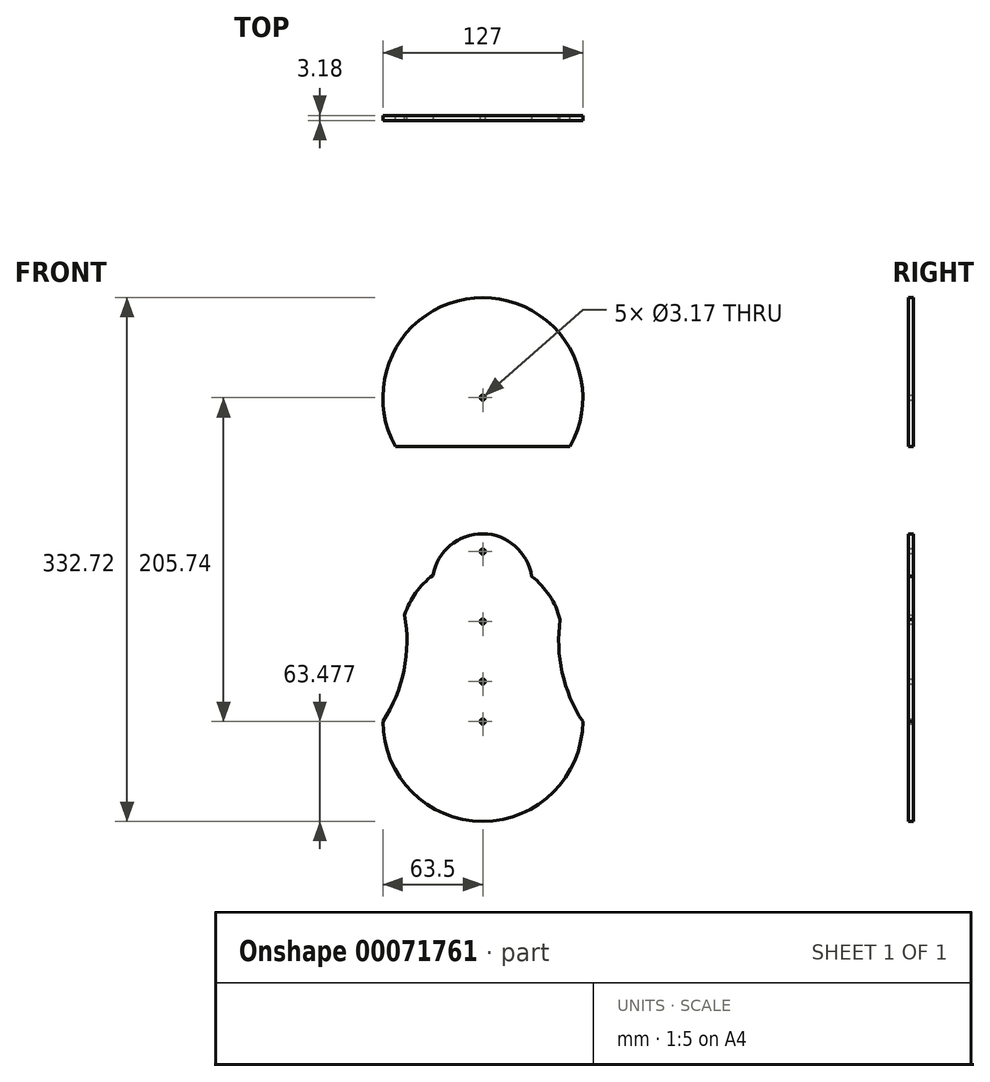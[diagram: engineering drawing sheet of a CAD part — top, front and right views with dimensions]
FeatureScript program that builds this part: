
annotation { "Feature Type Name" : "Feature", "Feature Type Description" : "" }
export const myFeature = defineFeature(function(context is Context, id is Id, definition is map)
    precondition{}
    {
        {
            var Q0;
            Q0=qCreatedBy(makeId("Front.planeOp"),FACE);
            var sketch = newSketch(context, id + "F0", { "sketchPlane" : qUnion([Q0])});
            skPoint(sketch, "E0.rect.middle", {"position": v(0, 0) * mm});
            skArc(sketch, "E1", {"start": v(63.5, 102.86) * mm, "mid": v(0, 166.36) * mm, "end": v(-63.5, 102.86) * mm});
            skArc(sketch, "E2", {"start": v(-63.5, -102.86) * mm, "mid": v(0, -166.36) * mm, "end": v(63.5, -102.86) * mm});
            skArc(sketch, "E3", {"start": v(-49.6, 35.1) * mm, "mid": v(-50.1, 70.3) * mm, "end": v(-63.5, 102.86) * mm});
            skArc(sketch, "E4", {"start": v(-63.5, -102.86) * mm, "mid": v(-50.1, -70.3) * mm, "end": v(-49.6, -35.1) * mm});
            skArc(sketch, "E5", {"start": v(63.5, 102.86) * mm, "mid": v(50.42, 71.84) * mm, "end": v(49.12, 38.2) * mm});
            skArc(sketch, "E6", {"start": v(49.12, -38.2) * mm, "mid": v(50.42, -71.84) * mm, "end": v(63.5, -102.86) * mm});
            skArc(sketch, "E7", {"start": v(48.18, -51.43) * mm, "mid": v(50.27, 0) * mm, "end": v(48.18, 51.43) * mm});
            skArc(sketch, "E8", {"start": v(-48.23, 54.55) * mm, "mid": v(-50.58, 0) * mm, "end": v(-48.23, -54.55) * mm});
            skPoint(sketch, "E9.orphan", {"position": v(-63.5, 0) * mm});
            skPoint(sketch, "E10.orphan", {"position": v(63.5, 0) * mm});
            skSolve(sketch);
        }
        {
            var Q0;
            {var subQ4=sQuery(id+"F0.wireOp",EDGE,"E1");Q0=makeQuery(id+"F0.imprint","IMPRINT",FACE,{"disambiguationData":[TD([[makeQuery(id+"F0.imprint","IMPRINT",EDGE,{"derivedFrom":subQ4}),1.0]])]});}
            extrude(context, id + "F1", {"entities" : qUnion([Q0]), "depth" : 3.17 * mm});
        }
        {
            var Q0;
            Q0=makeQuery(id+"F1.opExtrude","CAP_FACE",FACE,{"disambiguationData":[OSD([sQuery(id+"F0.wireOp",EDGE,"E1"),sQuery(id+"F0.wireOp",EDGE,"E2"),sQuery(id+"F0.wireOp",EDGE,"E3"),sQuery(id+"F0.wireOp",EDGE,"E4"),sQuery(id+"F0.wireOp",EDGE,"E5"),sQuery(id+"F0.wireOp",EDGE,"E6"),sQuery(id+"F0.wireOp",EDGE,"E7"),sQuery(id+"F0.wireOp",EDGE,"E8")])],"isStart":false});
            var sketch = newSketch(context, id + "F2", { "sketchPlane" : qUnion([Q0])});
            skArc(sketch, "E11.0", {"start": v(63.5, 102.86) * mm, "mid": v(0, 166.36) * mm, "end": v(-63.5, 102.86) * mm});
            skArc(sketch, "E12.0", {"start": v(-63.5, -102.86) * mm, "mid": v(0, -166.36) * mm, "end": v(63.5, -102.86) * mm});
            skCircle(sketch, "E13", {"center": v(0, 102.86) * mm, "radius": 31.75 * mm});
            skSolve(sketch);
        }
        {
            var Q0;
            Q0=makeQuery(id+"F2.imprint","IMPRINT",FACE,{"disambiguationData":[TD([[makeQuery(id+"F2.imprint","IMPRINT",EDGE,{"derivedFrom":sQuery(id+"F2.wireOp",EDGE,"E11.0")}),1.0]])]});
            var sketch = newSketch(context, id + "F3", { "sketchPlane" : qUnion([Q0])});
            skCircle(sketch, "E14.0", {"center": v(0, 102.86) * mm, "radius": 31.75 * mm});
            skCircle(sketch, "E15", {"center": v(0, 58.4) * mm, "radius": 12.7 * mm});
            skSolve(sketch);
        }
        {
            var Q0;
            Q0=makeQuery(id+"F2.imprint","IMPRINT",FACE,{"disambiguationData":[TD([[makeQuery(id+"F2.imprint","IMPRINT",EDGE,{"derivedFrom":sQuery(id+"F2.wireOp",EDGE,"E13")}),1.0]])]});
            extrude(context, id + "F4", {"entities" : qUnion([Q0]), "depth" : 6.35 * mm});
        }
        {
            var Q0;
            Q0=makeQuery(id+"F3.imprint","IMPRINT",FACE,{"disambiguationData":[TD([[makeQuery(id+"F3.imprint","IMPRINT",EDGE,{"derivedFrom":sQuery(id+"F3.wireOp",EDGE,"E15")}),1.0]])]});
            extrude(context, id + "F5", {"entities" : qUnion([Q0]), "depth" : 6.35 * mm});
        }
        {
            var Q0;
            Q0=makeQuery(id+"F5.opExtrude","CAP_FACE",FACE,{"disambiguationData":[OSD([sQuery(id+"F3.wireOp",EDGE,"E15")])],"isStart":false});
            var sketch = newSketch(context, id + "F6", { "sketchPlane" : qUnion([Q0])});
            skCircle(sketch, "E16.0", {"center": v(0, 58.4) * mm, "radius": 12.7 * mm});
            skCircle(sketch, "E17", {"center": v(0, 58.4) * mm, "radius": 40.64 * mm});
            skSolve(sketch);
        }
        {
            var Q0;
            Q0=makeQuery(id+"F6.imprint","IMPRINT",FACE,{"disambiguationData":[TD([[makeQuery(id+"F6.imprint","IMPRINT",EDGE,{"derivedFrom":sQuery(id+"F6.wireOp",EDGE,"E16.0")}),-1.0]])]});
            var Q1;
            Q1=makeQuery(id+"F6.imprint","IMPRINT",FACE,{"disambiguationData":[TD([[makeQuery(id+"F6.imprint","IMPRINT",EDGE,{"derivedFrom":sQuery(id+"F6.wireOp",EDGE,"E16.0")}),1.0]])]});
            extrude(context, id + "F7", {"entities" : qUnion([Q0, Q1]), "depth" : 6.35 * mm});
        }
        {
            var Q0;
            Q0=makeQuery(id+"F7.opExtrude","CAP_FACE",FACE,{"disambiguationData":[OSD([sQuery(id+"F6.wireOp",EDGE,"E17")])],"isStart":true});
            var sketch = newSketch(context, id + "F8", { "sketchPlane" : qUnion([Q0])});
            skCircle(sketch, "E18.0", {"center": v(0, 58.4) * mm, "radius": 40.64 * mm});
            skCircle(sketch, "E19", {"center": v(0, 5.07) * mm, "radius": 12.7 * mm});
            skSolve(sketch);
        }
        {
            var Q0;
            Q0=makeQuery(id+"F8.imprint","IMPRINT",FACE,{"disambiguationData":[TD([[makeQuery(id+"F8.imprint","IMPRINT",EDGE,{"derivedFrom":sQuery(id+"F8.wireOp",EDGE,"E19")}),1.0]])]});
            extrude(context, id + "F9", {"entities" : qUnion([Q0]), "operationType" : NewBodyOperationType.ADD, "oppositeDirection" : true, "depth" : 6.35 * mm});
        }
        {
            var Q0;
            Q0=makeQuery(id+"F9.opExtrude","CAP_FACE",FACE,{"disambiguationData":[OSD([sQuery(id+"F8.wireOp",EDGE,"E19")])],"isStart":true});
            var sketch = newSketch(context, id + "F10", { "sketchPlane" : qUnion([Q0])});
            skCircle(sketch, "E20", {"center": v(0, 5.07) * mm, "radius": 31.75 * mm});
            skSolve(sketch);
        }
        {
            var Q0;
            Q0=makeQuery(id+"F10.imprint","IMPRINT",FACE,{"disambiguationData":[TD([[makeQuery(id+"F10.imprint","IMPRINT",EDGE,{"derivedFrom":sQuery(id+"F10.wireOp",EDGE,"E20")}),1.0]])]});
            var Q1;
            Q1=makeQuery(id+"F10.imprint","IMPRINT",FACE,{"disambiguationData":[TD([[makeQuery(id+"F10.imprint","IMPRINT",EDGE,{"derivedFrom":makeQuery(id+"F9.opExtrude","CAP_EDGE",EDGE,{"disambiguationData":[OSD([sQuery(id+"F8.wireOp",EDGE,"E19")])],"isStart":true})}),1.0]])]});
            extrude(context, id + "F11", {"entities" : qUnion([Q0, Q1]), "depth" : 6.35 * mm});
        }
        {
            var Q0;
            Q0=makeQuery(id+"F1.opExtrude","CAP_FACE",FACE,{"disambiguationData":[OSD([sQuery(id+"F0.wireOp",EDGE,"E1"),sQuery(id+"F0.wireOp",EDGE,"E2"),sQuery(id+"F0.wireOp",EDGE,"E3"),sQuery(id+"F0.wireOp",EDGE,"E4"),sQuery(id+"F0.wireOp",EDGE,"E5"),sQuery(id+"F0.wireOp",EDGE,"E6"),sQuery(id+"F0.wireOp",EDGE,"E7"),sQuery(id+"F0.wireOp",EDGE,"E8")])],"isStart":false});
            var sketch = newSketch(context, id + "F12", { "sketchPlane" : qUnion([Q0])});
            skCircle(sketch, "E21.0", {"center": v(0, 5.07) * mm, "radius": 12.7 * mm});
            skCircle(sketch, "E22", {"center": v(0, -39.38) * mm, "radius": 12.7 * mm});
            skSolve(sketch);
        }
        {
            var Q0;
            Q0=makeQuery(id+"F12.imprint","IMPRINT",FACE,{"disambiguationData":[TD([[makeQuery(id+"F12.imprint","IMPRINT",EDGE,{"derivedFrom":sQuery(id+"F12.wireOp",EDGE,"E22")}),1.0]])]});
            extrude(context, id + "F13", {"entities" : qUnion([Q0]), "depth" : 6.35 * mm});
        }
        {
            var Q0;
            Q0=makeQuery(id+"F13.opExtrude","CAP_FACE",FACE,{"disambiguationData":[OSD([sQuery(id+"F12.wireOp",EDGE,"E22")])],"isStart":false});
            var sketch = newSketch(context, id + "F14", { "sketchPlane" : qUnion([Q0])});
            skCircle(sketch, "E23", {"center": v(0, -39.38) * mm, "radius": 25.4 * mm});
            skSolve(sketch);
        }
        {
            var Q0;
            Q0=makeQuery(id+"F14.imprint","IMPRINT",FACE,{"disambiguationData":[TD([[makeQuery(id+"F14.imprint","IMPRINT",EDGE,{"derivedFrom":sQuery(id+"F14.wireOp",EDGE,"E23")}),1.0]])]});
            var Q1;
            Q1=makeQuery(id+"F14.imprint","IMPRINT",FACE,{"disambiguationData":[TD([[makeQuery(id+"F14.imprint","IMPRINT",EDGE,{"derivedFrom":makeQuery(id+"F13.opExtrude","CAP_EDGE",EDGE,{"disambiguationData":[OSD([sQuery(id+"F12.wireOp",EDGE,"E22")])],"isStart":false})}),1.0]])]});
            extrude(context, id + "F15", {"entities" : qUnion([Q0, Q1]), "depth" : 6.35 * mm});
        }
        {
            var Q0;
            Q0=makeQuery(id+"F15.opExtrude","CAP_FACE",FACE,{"disambiguationData":[OSD([sQuery(id+"F14.wireOp",EDGE,"E23")])],"isStart":true});
            var sketch = newSketch(context, id + "F16", { "sketchPlane" : qUnion([Q0])});
            skCircle(sketch, "E24.0", {"center": v(0, -39.38) * mm, "radius": 25.4 * mm});
            skCircle(sketch, "E25", {"center": v(0, -77.48) * mm, "radius": 12.7 * mm});
            skSolve(sketch);
        }
        {
            var Q0;
            Q0=makeQuery(id+"F16.imprint","IMPRINT",FACE,{"disambiguationData":[TD([[makeQuery(id+"F16.imprint","IMPRINT",EDGE,{"derivedFrom":sQuery(id+"F16.wireOp",EDGE,"E25")}),1.0]])]});
            extrude(context, id + "F17", {"entities" : qUnion([Q0]), "oppositeDirection" : true, "depth" : 6.35 * mm});
        }
        {
            var Q0;
            Q0=makeQuery(id+"F17.opExtrude","CAP_FACE",FACE,{"disambiguationData":[OSD([sQuery(id+"F16.wireOp",EDGE,"E25")])],"isStart":true});
            var sketch = newSketch(context, id + "F18", { "sketchPlane" : qUnion([Q0])});
            skCircle(sketch, "E26.0", {"center": v(0, -77.48) * mm, "radius": 12.7 * mm});
            skCircle(sketch, "E27", {"center": v(0, -102.88) * mm, "radius": 12.7 * mm});
            skSolve(sketch);
        }
        {
            var Q0;
            Q0=makeQuery(id+"F18.imprint","IMPRINT",FACE,{"disambiguationData":[TD([[makeQuery(id+"F18.imprint","IMPRINT",EDGE,{"derivedFrom":sQuery(id+"F18.wireOp",EDGE,"E27")}),1.0]])]});
            extrude(context, id + "F19", {"entities" : qUnion([Q0]), "oppositeDirection" : true, "depth" : 6.35 * mm});
        }
        {
            var Q0;
            Q0=makeQuery(id+"F1.opExtrude","CAP_FACE",FACE,{"disambiguationData":[OSD([sQuery(id+"F0.wireOp",EDGE,"E1"),sQuery(id+"F0.wireOp",EDGE,"E2"),sQuery(id+"F0.wireOp",EDGE,"E3"),sQuery(id+"F0.wireOp",EDGE,"E4"),sQuery(id+"F0.wireOp",EDGE,"E5"),sQuery(id+"F0.wireOp",EDGE,"E6"),sQuery(id+"F0.wireOp",EDGE,"E7"),sQuery(id+"F0.wireOp",EDGE,"E8")])],"isStart":false});
            var sketch = newSketch(context, id + "F20", { "sketchPlane" : qUnion([Q0])});
            skCircle(sketch, "E28.0", {"center": v(0, -77.48) * mm, "radius": 12.7 * mm});
            skCircle(sketch, "E29", {"center": v(0, -77.48) * mm, "radius": 6.35 * mm});
            skCircle(sketch, "E30.0", {"center": v(0, -102.88) * mm, "radius": 12.7 * mm});
            skCircle(sketch, "E31", {"center": v(0, -102.88) * mm, "radius": 6.35 * mm});
            skSolve(sketch);
        }
        {
            var Q0;
            Q0=makeQuery(id+"F20.imprint","IMPRINT",FACE,{"disambiguationData":[TD([[makeQuery(id+"F20.imprint","IMPRINT",EDGE,{"derivedFrom":sQuery(id+"F20.wireOp",EDGE,"E29")}),1.0]])]});
            var Q1;
            Q1=makeQuery(id+"F20.imprint","IMPRINT",FACE,{"disambiguationData":[TD([[makeQuery(id+"F20.imprint","IMPRINT",EDGE,{"derivedFrom":sQuery(id+"F20.wireOp",EDGE,"E31")}),1.0]])]});
            extrude(context, id + "F21", {"entities" : qUnion([Q0, Q1]), "depth" : 6.35 * mm});
        }
        {
            var Q0;
            Q0=makeQuery(id+"F1.opExtrude","CAP_FACE",FACE,{"disambiguationData":[OSD([sQuery(id+"F0.wireOp",EDGE,"E1"),sQuery(id+"F0.wireOp",EDGE,"E2"),sQuery(id+"F0.wireOp",EDGE,"E3"),sQuery(id+"F0.wireOp",EDGE,"E4"),sQuery(id+"F0.wireOp",EDGE,"E5"),sQuery(id+"F0.wireOp",EDGE,"E6"),sQuery(id+"F0.wireOp",EDGE,"E7"),sQuery(id+"F0.wireOp",EDGE,"E8")])],"isStart":true});
            var sketch = newSketch(context, id + "F22", { "sketchPlane" : qUnion([Q0])});
            skCircle(sketch, "E32", {"center": v(0, 102.86) * mm, "radius": 1.59 * mm});
            skCircle(sketch, "E33", {"center": v(0, 58.4) * mm, "radius": 1.59 * mm});
            skCircle(sketch, "E34", {"center": v(0, 5.07) * mm, "radius": 1.59 * mm});
            skCircle(sketch, "E35", {"center": v(0, -39.38) * mm, "radius": 1.59 * mm});
            skCircle(sketch, "E36", {"center": v(0, -77.48) * mm, "radius": 1.59 * mm});
            skCircle(sketch, "E37", {"center": v(0, -102.88) * mm, "radius": 1.59 * mm});
            skSolve(sketch);
        }
        {
            var Q0;
            Q0=qSketchRegion(id+"F22",true);
            extrude(context, id + "F23", {"entities" : qUnion([Q0]), "operationType" : NewBodyOperationType.REMOVE, "endBound" : BoundingType.THROUGH_ALL, "oppositeDirection" : true, "depth" : 25.4 * mm});
        }
        {
            var Q0;
            Q0=makeQuery(id+"F1.opExtrude","CAP_FACE",FACE,{"disambiguationData":[OSD([sQuery(id+"F0.wireOp",EDGE,"E1"),sQuery(id+"F0.wireOp",EDGE,"E2"),sQuery(id+"F0.wireOp",EDGE,"E3"),sQuery(id+"F0.wireOp",EDGE,"E4"),sQuery(id+"F0.wireOp",EDGE,"E5"),sQuery(id+"F0.wireOp",EDGE,"E6"),sQuery(id+"F0.wireOp",EDGE,"E7"),sQuery(id+"F0.wireOp",EDGE,"E8")])],"isStart":true});
            var sketch = newSketch(context, id + "F24", { "sketchPlane" : qUnion([Q0])});
            skLineSegment(sketch, "E38", {"start": v(-50.42, 71.84) * mm, "end": v(50.42, 71.84) * mm});
            skLineSegment(sketch, "E39", {"start": v(-50.27, 0) * mm, "end": v(50.58, 0) * mm});
            skSolve(sketch);
        }
        {
            var Q0;
            Q0=makeQuery(id+"F4.opExtrude","SWEPT_BODY",BODY,{"disambiguationData":[OSD([sQuery(id+"F2.wireOp",EDGE,"E13")])]});
            deleteBodies(context, id + "F25", {"entities" : qUnion([Q0])});
        }
        {
            var Q0;
            Q0=makeQuery(id+"F7.opExtrude","SWEPT_BODY",BODY,{"disambiguationData":[OSD([sQuery(id+"F6.wireOp",EDGE,"E17")])]});
            deleteBodies(context, id + "F26", {"entities" : qUnion([Q0])});
        }
        {
            var Q0;
            Q0=makeQuery(id+"F5.opExtrude","SWEPT_BODY",BODY,{"disambiguationData":[OSD([sQuery(id+"F3.wireOp",EDGE,"E15")])]});
            deleteBodies(context, id + "F27", {"entities" : qUnion([Q0])});
        }
        {
            var Q0;
            Q0=makeQuery(id+"F9.opExtrude","SWEPT_BODY",BODY,{"disambiguationData":[OSD([sQuery(id+"F8.wireOp",EDGE,"E19")])]});
            deleteBodies(context, id + "F28", {"entities" : qUnion([Q0])});
        }
        {
            var Q0;
            Q0=makeQuery(id+"F11.opExtrude","SWEPT_BODY",BODY,{"disambiguationData":[OSD([sQuery(id+"F10.wireOp",EDGE,"E20")])]});
            deleteBodies(context, id + "F29", {"entities" : qUnion([Q0])});
        }
        {
            var Q0;
            Q0=makeQuery(id+"F15.opExtrude","SWEPT_BODY",BODY,{"disambiguationData":[OSD([sQuery(id+"F14.wireOp",EDGE,"E23")])]});
            deleteBodies(context, id + "F30", {"entities" : qUnion([Q0])});
        }
        {
            var Q0;
            Q0=makeQuery(id+"F13.opExtrude","SWEPT_BODY",BODY,{"disambiguationData":[OSD([sQuery(id+"F12.wireOp",EDGE,"E22")])]});
            deleteBodies(context, id + "F31", {"entities" : qUnion([Q0])});
        }
        {
            var Q0;
            Q0=makeQuery(id+"F17.opExtrude","SWEPT_BODY",BODY,{"disambiguationData":[OSD([sQuery(id+"F16.wireOp",EDGE,"E25")])]});
            deleteBodies(context, id + "F32", {"entities" : qUnion([Q0])});
        }
        {
            var Q0;
            Q0=makeQuery(id+"F21.opExtrude","SWEPT_BODY",BODY,{"disambiguationData":[OSD([sQuery(id+"F20.wireOp",EDGE,"E29")])]});
            deleteBodies(context, id + "F33", {"entities" : qUnion([Q0])});
        }
        {
            var Q0;
            Q0=makeQuery(id+"F19.opExtrude","SWEPT_BODY",BODY,{"disambiguationData":[OSD([sQuery(id+"F18.wireOp",EDGE,"E27")])]});
            deleteBodies(context, id + "F34", {"entities" : qUnion([Q0])});
        }
        {
            var Q0;
            Q0=makeQuery(id+"F21.opExtrude","SWEPT_BODY",BODY,{"disambiguationData":[OSD([sQuery(id+"F20.wireOp",EDGE,"E31")])]});
            deleteBodies(context, id + "F35", {"entities" : qUnion([Q0])});
        }
        {
            var Q0;
            {var subQ4=sQuery(id+"F24.wireOp",EDGE,"E38");Q0=makeQuery(id+"F24.imprint","IMPRINT",FACE,{"disambiguationData":[TD([[makeQuery(id+"F24.imprint","IMPRINT",EDGE,{"derivedFrom":subQ4}),-1.0]])]});}
            extrude(context, id + "F36", {"entities" : qUnion([Q0]), "operationType" : NewBodyOperationType.REMOVE, "oppositeDirection" : true, "depth" : 25.4 * mm});
        }
        {
            var Q0;
            {var subQ0=sQuery(id+"F0.wireOp",EDGE,"E6");var subQ1=sQuery(id+"F0.wireOp",EDGE,"E4");var subQ2=sQuery(id+"F0.wireOp",EDGE,"E7");var subQ3=sQuery(id+"F0.wireOp",EDGE,"E2");var subQ4=sQuery(id+"F0.wireOp",EDGE,"E8");Q0=makeQuery(id+"F36.boolean.opBoolean","SPLIT",FACE,{"disambiguationData":[TD([makeQuery(id+"F1.opExtrude","SWEPT_FACE",FACE,{"disambiguationData":[OSD([subQ3])]})])],"derivedFrom":makeQuery(id+"F1.opExtrude","CAP_FACE",FACE,{"disambiguationData":[OSD([sQuery(id+"F0.wireOp",EDGE,"E1"),subQ3,sQuery(id+"F0.wireOp",EDGE,"E3"),subQ1,sQuery(id+"F0.wireOp",EDGE,"E5"),subQ0,subQ2,subQ4])],"isStart":true})});}
            var sketch = newSketch(context, id + "F37", { "sketchPlane" : qUnion([Q0])});
            skArc(sketch, "E40", {"start": v(0.16, 0) * mm, "mid": v(-31.03, -10.65) * mm, "end": v(-49.12, -38.2) * mm});
            skArc(sketch, "E41", {"start": v(49.6, -35.1) * mm, "mid": v(30.7, -9.37) * mm, "end": v(0.16, 0) * mm});
            skSolve(sketch);
        }
        {
            var Q0;
            {var subQ1=makeQuery(id+"F1.opExtrude","CAP_EDGE",EDGE,{"disambiguationData":[OSD([sQuery(id+"F0.wireOp",EDGE,"E7")])],"isStart":true});Q0=makeQuery(id+"F37.imprint","IMPRINT",FACE,{"disambiguationData":[TD([[makeQuery(id+"F37.imprint","IMPRINT",EDGE,{"derivedFrom":subQ1}),-1.0]])]});}
            var Q1;
            {var subQ1=makeQuery(id+"F1.opExtrude","CAP_EDGE",EDGE,{"disambiguationData":[OSD([sQuery(id+"F0.wireOp",EDGE,"E8")])],"isStart":true});Q1=makeQuery(id+"F37.imprint","IMPRINT",FACE,{"disambiguationData":[TD([[makeQuery(id+"F37.imprint","IMPRINT",EDGE,{"derivedFrom":subQ1}),-1.0]])]});}
            extrude(context, id + "F38", {"entities" : qUnion([Q0, Q1]), "operationType" : NewBodyOperationType.REMOVE, "oppositeDirection" : true, "depth" : 25.4 * mm});
        }
        {
            var Q0;
            {var subQ0=sQuery(id+"F0.wireOp",EDGE,"E5");var subQ1=sQuery(id+"F0.wireOp",EDGE,"E3");var subQ2=sQuery(id+"F0.wireOp",EDGE,"E1");Q0=makeQuery(id+"F36.boolean.opBoolean","SPLIT",FACE,{"disambiguationData":[TD([makeQuery(id+"F1.opExtrude","SWEPT_FACE",FACE,{"disambiguationData":[OSD([subQ2])]})])],"derivedFrom":makeQuery(id+"F1.opExtrude","CAP_FACE",FACE,{"disambiguationData":[OSD([subQ2,sQuery(id+"F0.wireOp",EDGE,"E2"),subQ1,sQuery(id+"F0.wireOp",EDGE,"E4"),subQ0,sQuery(id+"F0.wireOp",EDGE,"E6"),sQuery(id+"F0.wireOp",EDGE,"E7"),sQuery(id+"F0.wireOp",EDGE,"E8")])],"isStart":true})});}
            var sketch = newSketch(context, id + "F39", { "sketchPlane" : qUnion([Q0])});
            skCircle(sketch, "E42.0", {"center": v(0, 102.86) * mm, "radius": 1.59 * mm});
            skArc(sketch, "E43.0.0", {"start": v(-63.5, 102.86) * mm, "mid": v(-55.56, 87.94) * mm, "end": v(-50.42, 71.84) * mm});
            skLineSegment(sketch, "E43.0.1", {"start": v(-50.42, 71.84) * mm, "end": v(50.42, 71.84) * mm});
            skArc(sketch, "E43.0.2", {"start": v(50.42, 71.84) * mm, "mid": v(55.56, 87.94) * mm, "end": v(63.5, 102.86) * mm});
            skArc(sketch, "E43.0.3", {"start": v(63.5, 102.86) * mm, "mid": v(0, 166.36) * mm, "end": v(-63.5, 102.86) * mm});
            skCircle(sketch, "E44", {"center": v(0, 102.86) * mm, "radius": 63.5 * mm});
            skLineSegment(sketch, "E45", {"start": v(-55.4, 71.84) * mm, "end": v(55.4, 71.84) * mm});
            skSolve(sketch);
        }
        {
            var Q0;
            {var subQ0=sQuery(id+"F39.wireOp",EDGE,"E43.0.0");Q0=makeQuery(id+"F39.imprint","IMPRINT",FACE,{"disambiguationData":[TD([[makeQuery(id+"F39.imprint","IMPRINT",EDGE,{"derivedFrom":subQ0}),-1.0]])]});}
            var Q1;
            {var subQ0=sQuery(id+"F39.wireOp",EDGE,"E43.0.2");Q1=makeQuery(id+"F39.imprint","IMPRINT",FACE,{"disambiguationData":[TD([[makeQuery(id+"F39.imprint","IMPRINT",EDGE,{"derivedFrom":subQ0}),-1.0]])]});}
            extrude(context, id + "F40", {"entities" : qUnion([Q0, Q1]), "operationType" : NewBodyOperationType.ADD, "oppositeDirection" : true, "depth" : 3.17 * mm});
        }
        {
            var Q0;
            {var subQ0=sQuery(id+"F0.wireOp",EDGE,"E6");var subQ1=sQuery(id+"F0.wireOp",EDGE,"E4");var subQ2=sQuery(id+"F0.wireOp",EDGE,"E7");var subQ3=sQuery(id+"F0.wireOp",EDGE,"E2");var subQ4=sQuery(id+"F0.wireOp",EDGE,"E8");Q0=makeQuery(id+"F36.boolean.opBoolean","SPLIT",FACE,{"disambiguationData":[TD([makeQuery(id+"F1.opExtrude","SWEPT_FACE",FACE,{"disambiguationData":[OSD([subQ3])]})])],"derivedFrom":makeQuery(id+"F1.opExtrude","CAP_FACE",FACE,{"disambiguationData":[OSD([sQuery(id+"F0.wireOp",EDGE,"E1"),subQ3,sQuery(id+"F0.wireOp",EDGE,"E3"),subQ1,sQuery(id+"F0.wireOp",EDGE,"E5"),subQ0,subQ2,subQ4])],"isStart":false})});}
            var sketch = newSketch(context, id + "F41", { "sketchPlane" : qUnion([Q0])});
            skArc(sketch, "E46", {"start": v(31.08, -10.69) * mm, "mid": v(0.01, 16.33) * mm, "end": v(-31.61, -10.03) * mm});
            skCircle(sketch, "E47.0", {"center": v(0, 5.07) * mm, "radius": 1.59 * mm});
            skSolve(sketch);
        }
        {
            var Q0;
            {var subQ0=sQuery(id+"F41.wireOp",EDGE,"E46");Q0=makeQuery(id+"F41.imprint","IMPRINT",FACE,{"disambiguationData":[TD([[makeQuery(id+"F41.imprint","IMPRINT",EDGE,{"derivedFrom":subQ0}),1.0]])]});}
            extrude(context, id + "F42", {"entities" : qUnion([Q0]), "operationType" : NewBodyOperationType.ADD, "oppositeDirection" : true, "depth" : 3.17 * mm});
        }
    });
